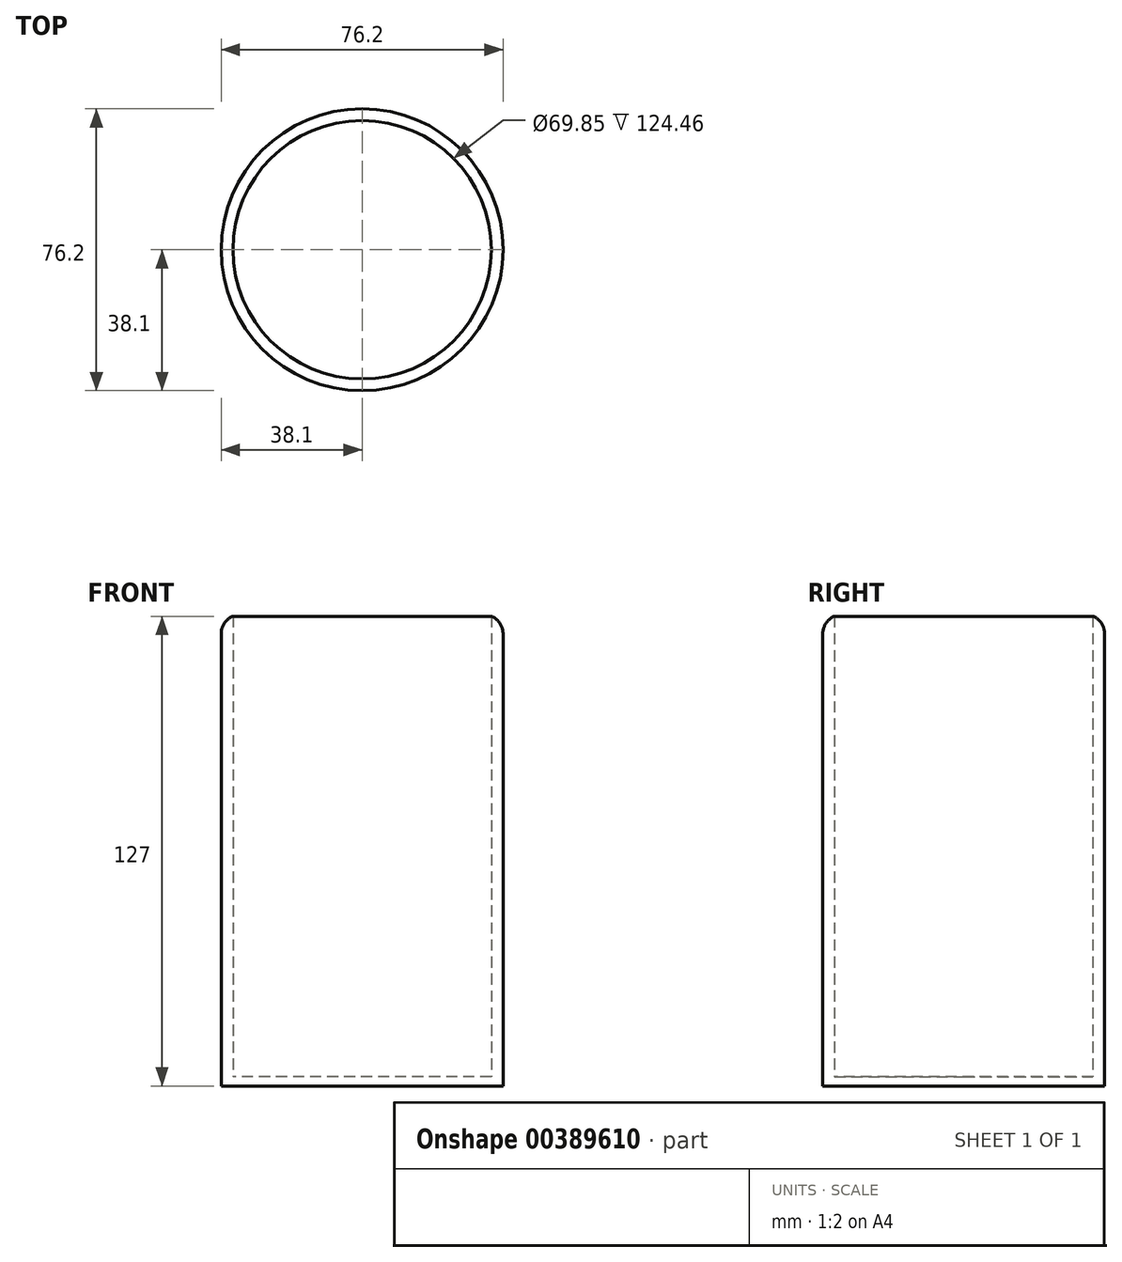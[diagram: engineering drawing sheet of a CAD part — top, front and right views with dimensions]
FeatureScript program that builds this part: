
annotation { "Feature Type Name" : "Feature", "Feature Type Description" : "" }
export const myFeature = defineFeature(function(context is Context, id is Id, definition is map)
    precondition{}
    {
        {
            var Q0;
            Q0=qCreatedBy(makeId("Top.planeOp"),FACE);
            var sketch = newSketch(context, id + "F0", { "sketchPlane" : qUnion([Q0])});
            skCircle(sketch, "E0", {"center": v(0, 0) * mm, "radius": 38.1 * mm});
            skCircle(sketch, "E1", {"center": v(0, 0) * mm, "radius": 34.93 * mm});
            skSolve(sketch);
        }
        {
            var Q0;
            Q0 = qSketchRegion(id + "F0", true);
            extrude(context, id + "F1", {"entities" : qUnion([Q0]), "depth" : 127 * mm});
        }
        {
            var Q0;
            Q0=qCreatedBy(makeId("Top.planeOp"),FACE);
            var sketch = newSketch(context, id + "F2", { "sketchPlane" : qUnion([Q0])});
            skCircle(sketch, "E2", {"center": v(0, 0) * mm, "radius": 34.92 * mm});
            skSolve(sketch);
        }
        {
            var Q0;
            Q0 = qSketchRegion(id + "F2", true);
            extrude(context, id + "F3", {"entities" : qUnion([Q0]), "operationType" : NewBodyOperationType.ADD, "depth" : 2.54 * mm});
        }
        {
            var Q0;
            Q0=makeQuery(id+"F1.opExtrude","CAP_EDGE",EDGE,{"disambiguationData":[OSD([sQuery(id+"F0.wireOp",EDGE,"E0")])],"isStart":false});
            fillet(context, id + "F4", {"entities" : qUnion([Q0]), "radius" : 5.08 * mm, "tangentPropagation" : true, "allowEdgeOverflow" : false});
        }
    });
